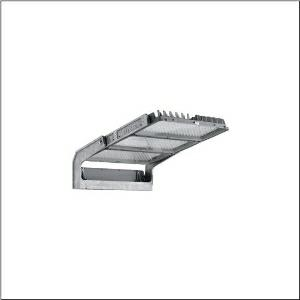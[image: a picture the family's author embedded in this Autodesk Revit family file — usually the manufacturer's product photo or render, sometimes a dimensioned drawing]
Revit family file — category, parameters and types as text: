
# Revit family: floodlight_fl_11_maxi_pro___rs07_5xa779124k01gb_d181
name_source: partatom
category: Lighting Fixtures
units: mm (PartAtom-declared; Revit-internal decimal feet)

## family parameters
Cut with Voids When Loaded = No
Host = Face
Light Source = No
Part Type = Normal
Room Calculation Point = No
Round Connector Dimension = Use Diameter
Shared = No

## types (1)
- --- (1 x LED, 123000 lm, 1227.1 W, 5700K)
    Apparent Load = 1227 VA
    CIE Flux Codes = 80 93 99 100 99
    Color Rendering = 90
    Color Temperature = 5700K
    Default Elevation = 1800 mm
    Description = Floodlight FL 11  maxi  pro floodlight; light control with lens of PMMA; cover panel of toughened safety glass, transparent; light distribution: RS07, rotationally symmetric direct distribution, LEDcolour temperature: 5700K, rated luminous flux: 123.000lm, colour rendering: CRI > 90, light colour: 957; luminous efficacy: 100lm/W; brightness control: DALI 2; with terminal, 5-pole, max. 2.5mm², mains connection: 220..240V/380..400V AC, 50/60Hz, surge voltage resistance: line to ground: 10kV, service life up to 100,000h L90. Typical operating time: 1000h per year, ECG replaceable separately, LED unit replaceable without ESD environment, dustproof LED module, dimming range 10..100%; 1227W floodlight with 3x LED unit of diecast aluminium, coated grey; length: 1.003mm / width: 651mm / height: 338mm; mounting bracket, of diecast aluminium, uncoated, natural, protection rating (complete): IP66; insulation class (complete): insulation class I (protective earthing); certification: CE, ENEC, VDE; ball protection: ball impact resistant, only for outdoor installations in the designated locations, permissible operating ambient temperature: -45..+55°C, permissible storage temperature: -40..+85°Cpackaging unit: 1 piece

Light Distribution: RS07
    Height = 320 mm
    Lamp = 1 x LED
    Lamp Light Flux = 123000 lm
    Lamp Power = 1227.1 W
    Lamp count = 1
    Length = 1002 mm
    Luminous efficacy = 100 lm/W
    Manufacturer = Siteco
    ModVariant = No
    Model = 5XA779124K01GB
    Mounting Place = Ceiling
    Mounting Type = Surface mounted
    Number of Poles = 1
    OnlyDefault = Yes
    Power Factor = 1
    Product Name = Floodlight FL 11 maxi pro | RS07
    Product group = floodlight | ceiling mounted
    ProductGroupID = 301
    Protection Class = Protection class I
    Protection Degree = IP 66
    RLX_Detail_Level = 1
    RLX_Emergency_Light_Flux = 0 lm
    RLX_Emergency_Type = 0
    RLX_Emergency_Type_DB = No
    RlxData = <blob elided: 40197 chars, md5=6412d2a8>
    Socket = socket
    Standby Power = 0 W
    System Light Flux = 123000 lm
    System Power = 1227 W
    Type Comments = factory setting: luminous flux: 100 % | dim-lin: 254 | 840 mA
    Type Image = l_1356210.jpg
    URL = http://relux.com
    VarID = @adj_023752
    Voltage = 0 V
    Weight = 0.00 kg
    Width = 655 mm

## geometry (parser evidence)
native form markers: Blend x4, Sweep x10
no freeform markers — native parametric forms only
